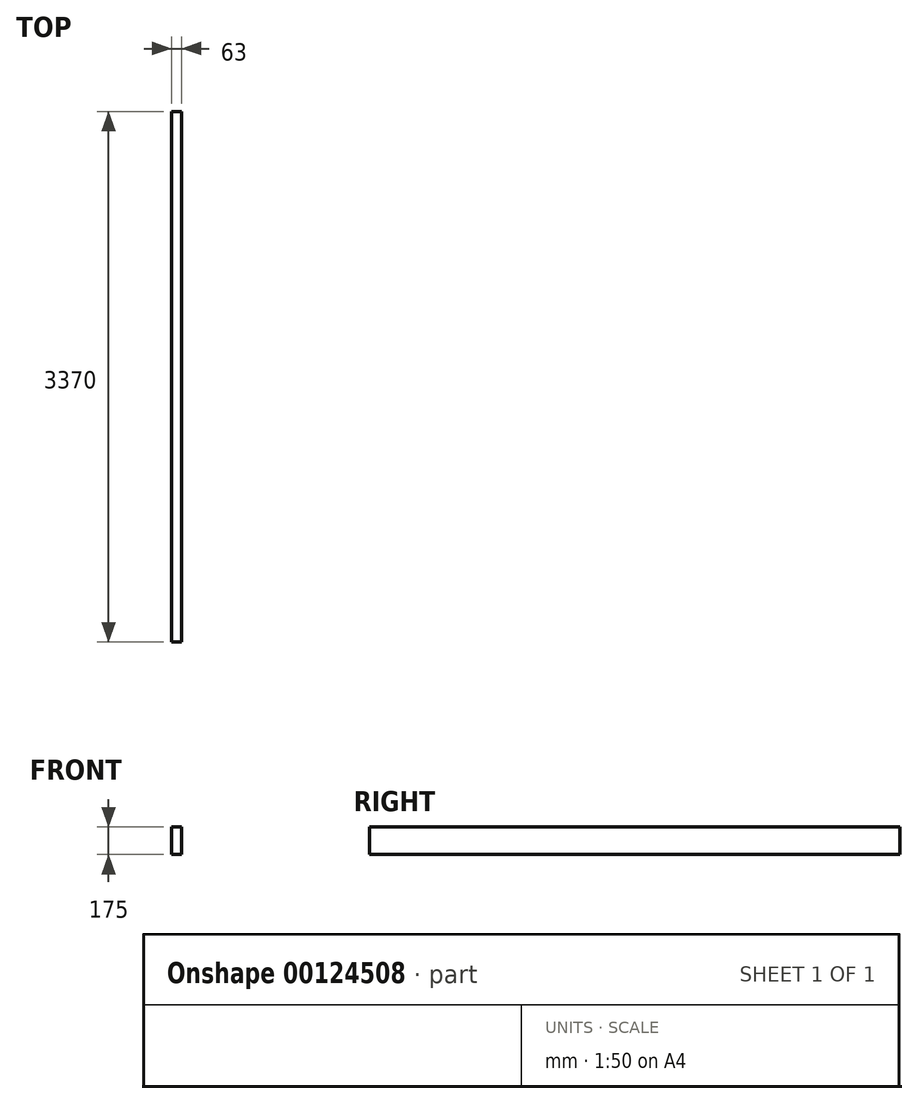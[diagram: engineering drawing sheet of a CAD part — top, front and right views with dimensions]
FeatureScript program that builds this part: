
annotation { "Feature Type Name" : "Feature", "Feature Type Description" : "" }
export const myFeature = defineFeature(function(context is Context, id is Id, definition is map)
    precondition{}
    {
        {
            var Q0;
            Q0=qCreatedBy(makeId("Front.planeOp"),FACE);
            var sketch = newSketch(context, id + "F0", { "sketchPlane" : qUnion([Q0])});
            skLineSegment(sketch, "E0.bottom", {"start": v(31.5, 87.5) * mm, "end": v(-31.5, 87.5) * mm});
            skLineSegment(sketch, "E0.top", {"start": v(31.5, -87.5) * mm, "end": v(-31.5, -87.5) * mm});
            skLineSegment(sketch, "E0.left", {"start": v(31.5, 87.5) * mm, "end": v(31.5, -87.5) * mm});
            skLineSegment(sketch, "E0.right", {"start": v(-31.5, 87.5) * mm, "end": v(-31.5, -87.5) * mm});
            skPoint(sketch, "E0.middle", {"position": v(0, 0) * mm});
            skSolve(sketch);
        }
        {
            var Q0;
            Q0=qSketchRegion(id+"F0",true);
            extrude(context, id + "F1", {"entities" : qUnion([Q0]), "endBound" : BoundingType.SYMMETRIC, "depth" : (3000 + 240 + 130) * mm});
        }
    });
